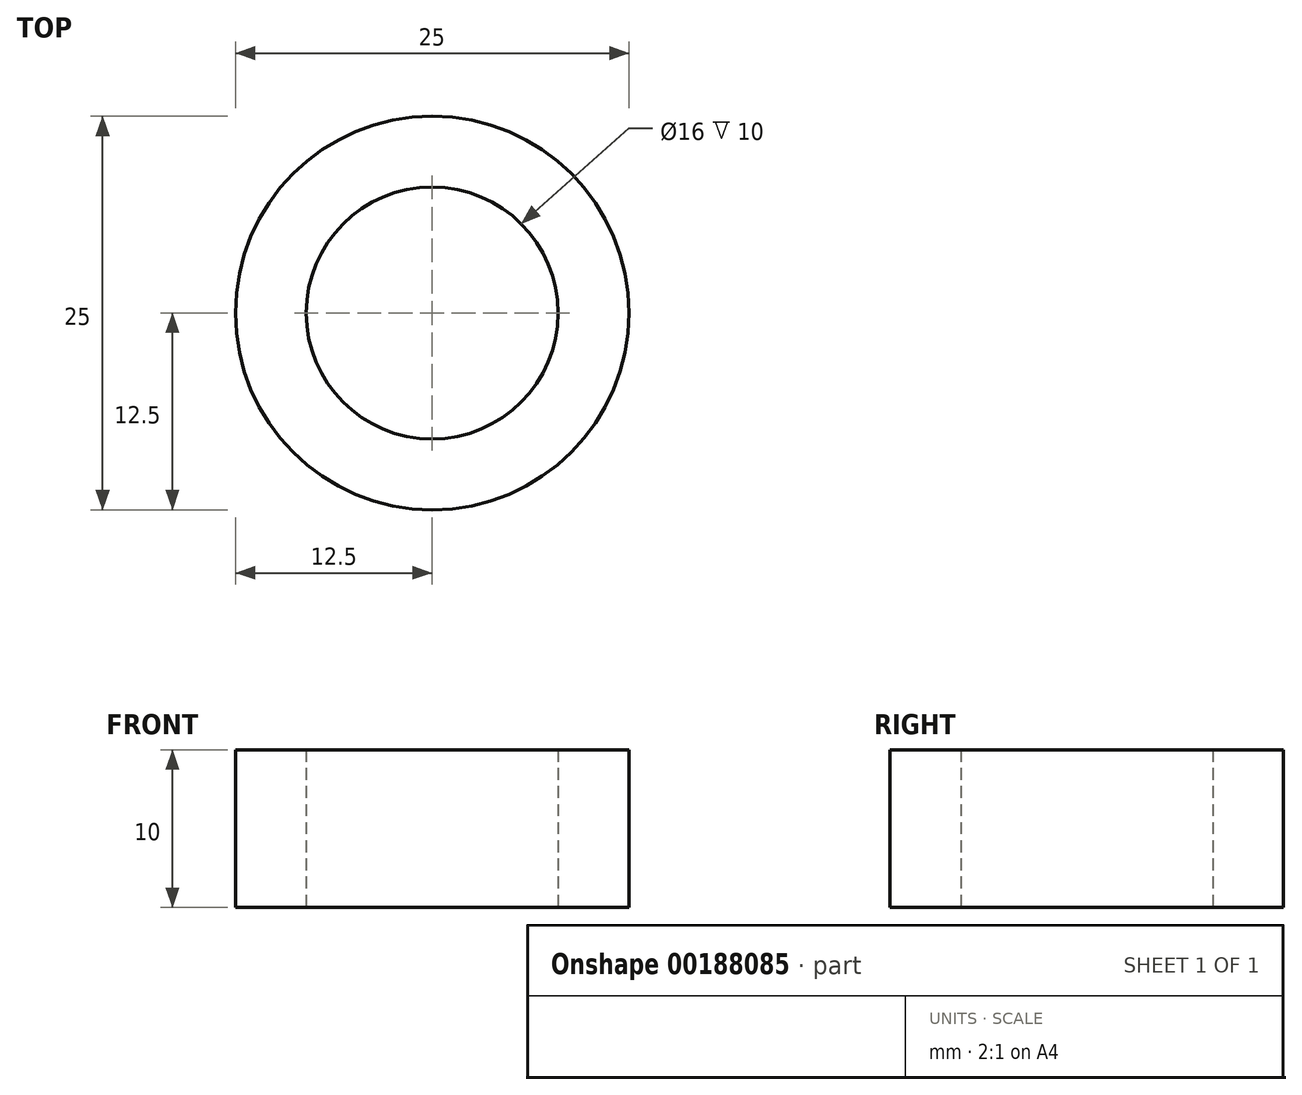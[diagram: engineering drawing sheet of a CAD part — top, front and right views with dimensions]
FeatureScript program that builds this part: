
annotation { "Feature Type Name" : "Feature", "Feature Type Description" : "" }
export const myFeature = defineFeature(function(context is Context, id is Id, definition is map)
    precondition{}
    {
        {
            var Q0;
            Q0=qCreatedBy(makeId("Top.planeOp"),FACE);
            var sketch = newSketch(context, id + "F0", { "sketchPlane" : qUnion([Q0])});
            skCircle(sketch, "E0", {"center": v(0, 0) * mm, "radius": 12.5 * mm});
            skCircle(sketch, "E1", {"center": v(0, 0) * mm, "radius": 8 * mm});
            skSolve(sketch);
        }
        {
            var Q0;
            Q0=makeQuery(id+"F0.imprint","IMPRINT",FACE,{"disambiguationData":[TD([[makeQuery(id+"F0.imprint","IMPRINT",EDGE,{"derivedFrom":sQuery(id+"F0.wireOp",EDGE,"E0")}),1.0]])]});
            extrude(context, id + "F1", {"entities" : qUnion([Q0]), "depth" : 10 * mm});
        }
    });
